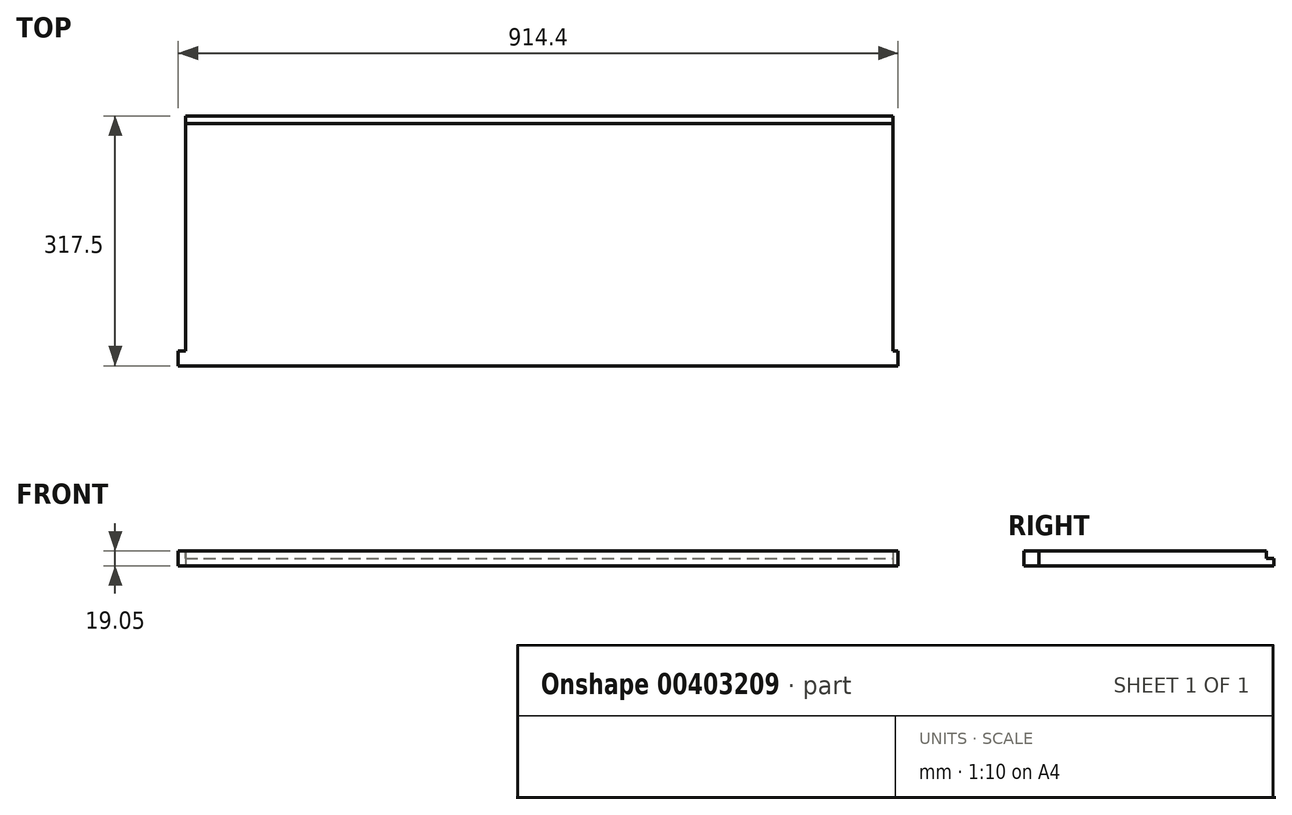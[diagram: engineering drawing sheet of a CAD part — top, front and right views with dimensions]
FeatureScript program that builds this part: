
annotation { "Feature Type Name" : "Feature", "Feature Type Description" : "" }
export const myFeature = defineFeature(function(context is Context, id is Id, definition is map)
    precondition{}
    {
        {
            var Q0;
            Q0=qCreatedBy(makeId("Top.planeOp"),FACE);
            var sketch = newSketch(context, id + "F0", { "sketchPlane" : qUnion([Q0])});
            skLineSegment(sketch, "E0.bottom", {"start": v(449.26, -158.75) * mm, "end": v(-449.26, -158.75) * mm});
            skLineSegment(sketch, "E0.top", {"start": v(449.26, 158.75) * mm, "end": v(-449.26, 158.75) * mm});
            skLineSegment(sketch, "E0.left", {"start": v(449.26, -158.75) * mm, "end": v(449.26, 158.75) * mm});
            skLineSegment(sketch, "E0.right", {"start": v(-449.26, -158.75) * mm, "end": v(-449.26, 158.75) * mm});
            skPoint(sketch, "E0.middle", {"position": v(0, 0) * mm});
            skSolve(sketch);
        }
        {
            var Q0;
            Q0=qSketchRegion(id+"F0",true);
            extrude(context, id + "F1", {"entities" : qUnion([Q0]), "depth" : 19.05 * mm});
        }
        {
            var Q0;
            Q0=makeQuery(id+"F1.opExtrude","SWEPT_FACE",FACE,{"disambiguationData":[OSD([sQuery(id+"F0.wireOp",EDGE,"E0.left")])]});
            var sketch = newSketch(context, id + "F2", { "sketchPlane" : qUnion([Q0])});
            skLineSegment(sketch, "E1.bottom", {"start": v(149.22, 19.05) * mm, "end": v(158.75, 19.05) * mm});
            skLineSegment(sketch, "E1.top", {"start": v(149.22, 9.52) * mm, "end": v(158.75, 9.52) * mm});
            skLineSegment(sketch, "E1.left", {"start": v(149.22, 19.05) * mm, "end": v(149.22, 9.52) * mm});
            skLineSegment(sketch, "E1.right", {"start": v(158.75, 19.05) * mm, "end": v(158.75, 9.52) * mm});
            skSolve(sketch);
        }
        {
            var Q0;
            Q0=qSketchRegion(id+"F2",true);
            extrude(context, id + "F3", {"entities" : qUnion([Q0]), "operationType" : NewBodyOperationType.REMOVE, "endBound" : BoundingType.THROUGH_ALL, "oppositeDirection" : true, "depth" : 25.4 * mm});
        }
        {
            var Q0;
            Q0=makeQuery(id+"F1.opExtrude","SWEPT_FACE",FACE,{"disambiguationData":[OSD([sQuery(id+"F0.wireOp",EDGE,"E0.right")])]});
            var sketch = newSketch(context, id + "F4", { "sketchPlane" : qUnion([Q0])});
            skLineSegment(sketch, "E2.bottom", {"start": v(158.75, 19.05) * mm, "end": v(139.7, 19.05) * mm});
            skLineSegment(sketch, "E2.top", {"start": v(158.75, 0) * mm, "end": v(139.7, 0) * mm});
            skLineSegment(sketch, "E2.left", {"start": v(158.75, 19.05) * mm, "end": v(158.75, 0) * mm});
            skLineSegment(sketch, "E2.right", {"start": v(139.7, 19.05) * mm, "end": v(139.7, 0) * mm});
            skSolve(sketch);
        }
        {
            var Q0;
            Q0 = qSketchRegion(id + "F4", true);
            extrude(context, id + "F5", {"entities" : qUnion([Q0]), "operationType" : NewBodyOperationType.ADD, "depth" : 9.52 * mm});
        }
        {
            var Q0;
            Q0=makeQuery(id+"F1.opExtrude","SWEPT_FACE",FACE,{"disambiguationData":[OSD([sQuery(id+"F0.wireOp",EDGE,"E0.left")])]});
            var sketch = newSketch(context, id + "F6", { "sketchPlane" : qUnion([Q0])});
            skLineSegment(sketch, "E3.0.0", {"start": v(-158.75, 19.05) * mm, "end": v(-139.7, 19.05) * mm});
            skLineSegment(sketch, "E3.0.1", {"start": v(-139.7, 19.05) * mm, "end": v(-139.7, 0) * mm});
            skLineSegment(sketch, "E3.0.2", {"start": v(-139.7, 0) * mm, "end": v(-158.75, 0) * mm});
            skLineSegment(sketch, "E3.0.3", {"start": v(-158.75, 0) * mm, "end": v(-158.75, 19.05) * mm});
            skSolve(sketch);
        }
        {
            var Q0;
            Q0 = qSketchRegion(id + "F6", true);
            extrude(context, id + "F7", {"entities" : qUnion([Q0]), "operationType" : NewBodyOperationType.ADD, "depth" : 6.35 * mm});
        }
    });
